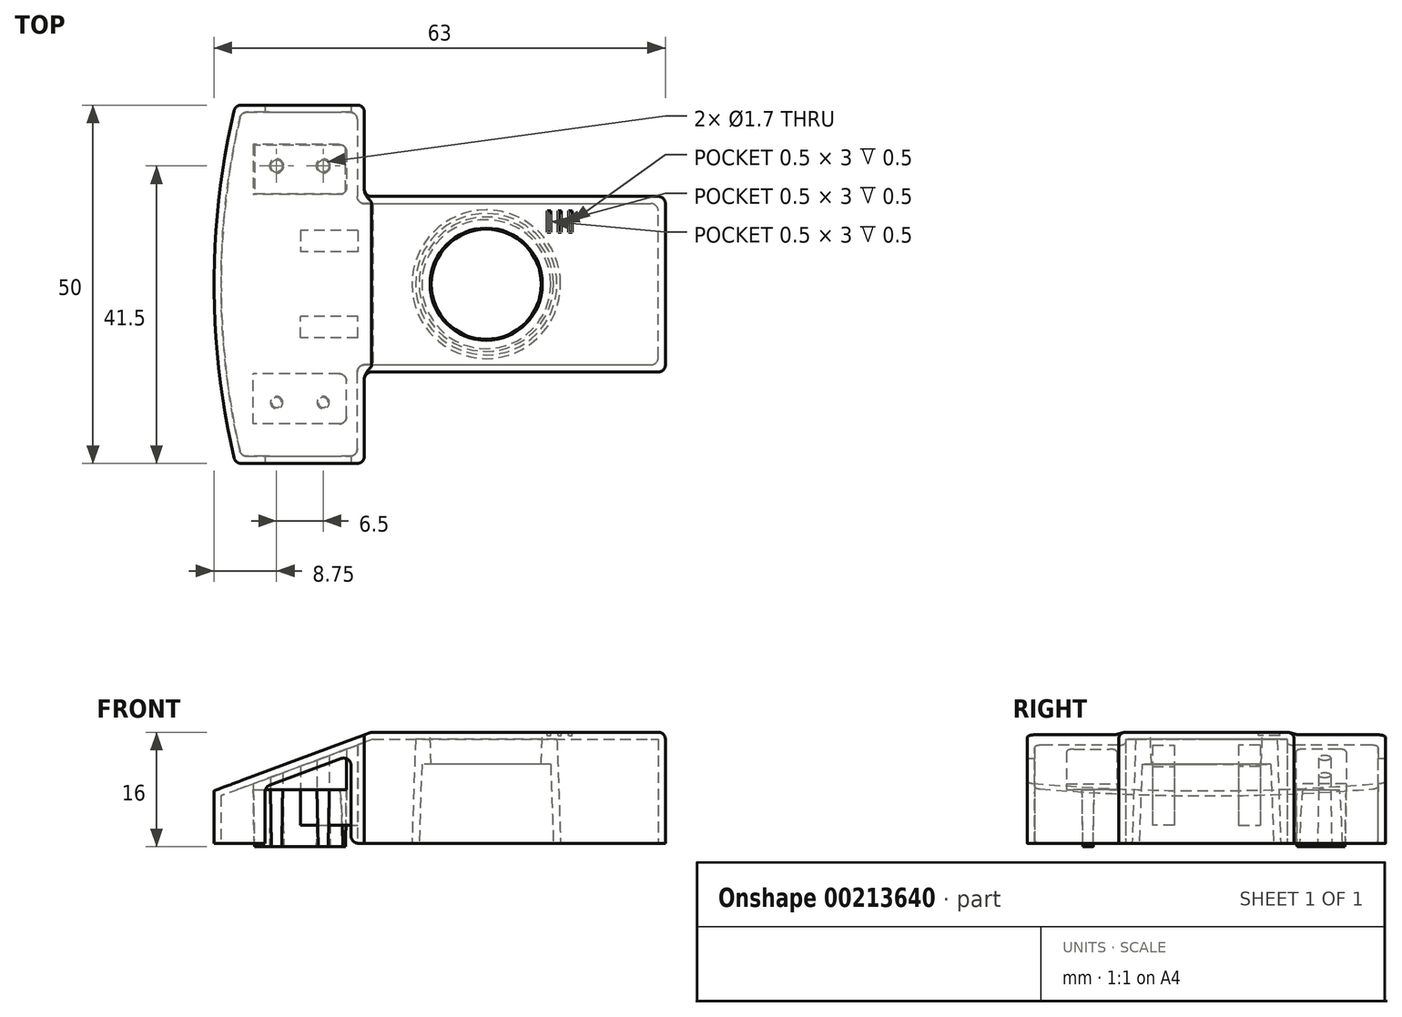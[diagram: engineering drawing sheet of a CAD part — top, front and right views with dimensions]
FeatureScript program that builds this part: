
annotation { "Feature Type Name" : "Feature", "Feature Type Description" : "" }
export const myFeature = defineFeature(function(context is Context, id is Id, definition is map)
    precondition{}
    {
        {
            var Q0;
            Q0=qCreatedBy(makeId("Top.planeOp"),FACE);
            var sketch = newSketch(context, id + "F0", { "sketchPlane" : qUnion([Q0])});
            skCircle(sketch, "E0", {"center": v(-4, 0) * mm, "radius": 9.37 * mm});
            skLineSegment(sketch, "E1.bottom", {"start": v(-21, -12.25) * mm, "end": v(21, -12.25) * mm});
            skLineSegment(sketch, "E1.top", {"start": v(-21, 12.25) * mm, "end": v(21, 12.25) * mm});
            skLineSegment(sketch, "E1.right", {"start": v(21, -12.25) * mm, "end": v(21, 12.25) * mm});
            skLineSegment(sketch, "E2.bottom", {"start": v(-21, -25) * mm, "end": v(-39, -25) * mm});
            skLineSegment(sketch, "E2.top", {"start": v(-21, 25) * mm, "end": v(-39, 25) * mm});
            skLineSegment(sketch, "E2.left", {"start": v(-21, -25) * mm, "end": v(-21, -12.25) * mm});
            skLineSegment(sketch, "E2.right", {"start": v(-39, -25) * mm, "end": v(-39, 25) * mm});
            skPoint(sketch, "E2.middle", {"position": v(-30, 0) * mm});
            skLineSegment(sketch, "E3.trimOffspring", {"start": v(-21, 12.25) * mm, "end": v(-21, 25) * mm});
            skLineSegment(sketch, "E4", {"start": v(-20, 12.25) * mm, "end": v(-20, -12.25) * mm});
            skPoint(sketch, "E5", {"position": v(-42, 0) * mm});
            skPoint(sketch, "E5.positionSnap0", {"position": v(-39, 0) * mm});
            skArc(sketch, "E6", {"start": v(-39, 25) * mm, "mid": v(-42, 0) * mm, "end": v(-39, -25) * mm});
            skSolve(sketch);
        }
        {
            var Q0;
            Q0=qSketchRegion(id+"F0",true);
            var Q1;
            Q1=makeQuery(id+"F0.imprint","IMPRINT",FACE,{"disambiguationData":[TD([[makeQuery(id+"F0.imprint","IMPRINT",EDGE,{"derivedFrom":sQuery(id+"F0.wireOp",EDGE,"E0")}),1.0]])]});
            extrude(context, id + "F1", {"entities" : qUnion([Q0, Q1]), "depth" : 15.5 * mm});
        }
        {
            var Q0;
            Q0=makeQuery(id+"F0.imprint","IMPRINT",FACE,{"disambiguationData":[TD([[makeQuery(id+"F0.imprint","IMPRINT",EDGE,{"derivedFrom":sQuery(id+"F0.wireOp",EDGE,"E0")}),1.0]])]});
            var Q1;
            Q1=makeQuery(id+"F1.opExtrude","CAP_FACE",FACE,{"disambiguationData":[OSD([sQuery(id+"F0.wireOp",EDGE,"E1.bottom"),sQuery(id+"F0.wireOp",EDGE,"E1.top"),sQuery(id+"F0.wireOp",EDGE,"E1.right"),sQuery(id+"F0.wireOp",EDGE,"E2.bottom"),sQuery(id+"F0.wireOp",EDGE,"E2.top"),sQuery(id+"F0.wireOp",EDGE,"E2.left"),sQuery(id+"F0.wireOp",EDGE,"E3.trimOffspring"),sQuery(id+"F0.wireOp",EDGE,"E6")])],"isStart":false});
            extrude(context, id + "F2", {"entities" : qUnion([Q0]), "operationType" : NewBodyOperationType.REMOVE, "endBound" : BoundingType.UP_TO_SURFACE, "endBoundEntityFace" : qUnion([Q1]), "depth" : 25 * mm, "hasDraft" : true, "draftAngle" : 2 * degree, "draftPullDirection" : true});
        }
        {
            var Q0;
            Q0=qCreatedBy(makeId("Front.planeOp"),FACE);
            var Q1;
            Q1=makeQuery(id+"F1.opExtrude","CAP_EDGE",EDGE,{"disambiguationData":[OSD([sQuery(id+"F0.wireOp",EDGE,"E2.bottom")])],"isStart":true});
            cPlane(context, id + "F3", {"entities" : qUnion([Q0, Q1]), "cplaneType" : CPlaneType.LINE_ANGLE, "offset" : 25 * mm, "angle" : 0 * degree, "width" : 150 * mm, "height" : 150 * mm});
        }
        {
            var Q0;
            Q0=qCreatedBy(id+"F3.planeOp",FACE);
            var sketch = newSketch(context, id + "F4", { "sketchPlane" : qUnion([Q0])});
            skLineSegment(sketch, "E7", {"start": v(20, 15.5) * mm, "end": v(42, 15.5) * mm});
            skLineSegment(sketch, "E8", {"start": v(42, 15.5) * mm, "end": v(42, 7.32) * mm});
            skLineSegment(sketch, "E9", {"start": v(42, 7.32) * mm, "end": v(20, 15.5) * mm});
            skLineSegment(sketch, "E10", {"start": v(42, 0) * mm, "end": v(41.46, 15.5) * mm, "construction": true});
            skLineSegment(sketch, "E11", {"start": v(42, 0) * mm, "end": v(42, 27.73) * mm, "construction": true});
            skSolve(sketch);
        }
        {
            var Q0;
            Q0=qSketchRegion(id+"F4",true);
            extrude(context, id + "F5", {"entities" : qUnion([Q0]), "operationType" : NewBodyOperationType.REMOVE, "endBound" : BoundingType.THROUGH_ALL, "depth" : 25 * mm});
        }
        {
            var Q0;
            Q0=makeQuery(id+"F1.opExtrude","CAP_FACE",FACE,{"disambiguationData":[OSD([sQuery(id+"F0.wireOp",EDGE,"E1.bottom"),sQuery(id+"F0.wireOp",EDGE,"E1.top"),sQuery(id+"F0.wireOp",EDGE,"E1.right"),sQuery(id+"F0.wireOp",EDGE,"E2.bottom"),sQuery(id+"F0.wireOp",EDGE,"E2.top"),sQuery(id+"F0.wireOp",EDGE,"E2.left"),sQuery(id+"F0.wireOp",EDGE,"E3.trimOffspring"),sQuery(id+"F0.wireOp",EDGE,"E6")])],"isStart":true});
            shell(context, id + "F6", {"entities" : qUnion([Q0]), "thickness" : 1 * mm});
        }
        {
            var Q0;
            Q0=makeQuery(id+"F1.opExtrude","SWEPT_FACE",FACE,{"disambiguationData":[OSD([sQuery(id+"F0.wireOp",EDGE,"E2.bottom")])]});
            var sketch = newSketch(context, id + "F7", { "sketchPlane" : qUnion([Q0])});
            skLineSegment(sketch, "E12", {"start": v(-20, 15.5) * mm, "end": v(-39, 8.43) * mm});
            skLineSegment(sketch, "E13", {"start": v(-39, 8.43) * mm, "end": v(-39, 15.5) * mm});
            skLineSegment(sketch, "E14", {"start": v(-39, 15.5) * mm, "end": v(-20, 15.5) * mm});
            skLineSegment(sketch, "E15", {"start": v(-34.87, 0) * mm, "end": v(-34.87, 7.86) * mm});
            skLineSegment(sketch, "E16", {"start": v(-34.87, 7.86) * mm, "end": v(-22.87, 12.32) * mm});
            skLineSegment(sketch, "E17", {"start": v(-22.87, 0) * mm, "end": v(-34.87, 0) * mm});
            skLineSegment(sketch, "E18", {"start": v(-22.87, 12.32) * mm, "end": v(-22.87, 0) * mm});
            skSolve(sketch);
        }
        {
            var Q0;
            Q0=makeQuery(id+"F7.imprint","IMPRINT",FACE,{"disambiguationData":[TD([[makeQuery(id+"F7.imprint","IMPRINT",EDGE,{"derivedFrom":sQuery(id+"F7.wireOp",EDGE,"E15")}),-1.0]])]});
            extrude(context, id + "F8", {"entities" : qUnion([Q0]), "operationType" : NewBodyOperationType.REMOVE, "endBound" : BoundingType.THROUGH_ALL, "oppositeDirection" : true, "depth" : 25 * mm});
        }
        {
            var Q0;
            Q0=makeQuery(id+"F1.opExtrude","CAP_FACE",FACE,{"disambiguationData":[OSD([sQuery(id+"F0.wireOp",EDGE,"E0"),sQuery(id+"F0.wireOp",EDGE,"E1.bottom"),sQuery(id+"F0.wireOp",EDGE,"E1.top"),sQuery(id+"F0.wireOp",EDGE,"E1.right"),sQuery(id+"F0.wireOp",EDGE,"E2.bottom"),sQuery(id+"F0.wireOp",EDGE,"E2.top"),sQuery(id+"F0.wireOp",EDGE,"E2.left"),sQuery(id+"F0.wireOp",EDGE,"E2.right"),sQuery(id+"F0.wireOp",EDGE,"E3.trimOffspring")])],"isStart":false});
            cPlane(context, id + "F9", {"entities" : qUnion([Q0]), "cplaneType" : CPlaneType.OFFSET, "offset" : 8 * mm, "oppositeDirection" : true, "width" : 150 * mm, "height" : 150 * mm});
        }
        {
            var Q0;
            Q0=qCreatedBy(id+"F9.planeOp",FACE);
            var sketch = newSketch(context, id + "F10", { "sketchPlane" : qUnion([Q0])});
            skLineSegment(sketch, "E19", {"start": v(0, 0) * mm, "end": v(-63, 0) * mm, "construction": true});
            skLineSegment(sketch, "E20.bottom", {"start": v(-36.5, -12.5) * mm, "end": v(-23.5, -12.5) * mm});
            skLineSegment(sketch, "E20.top", {"start": v(-36.5, -19.5) * mm, "end": v(-23.5, -19.5) * mm});
            skLineSegment(sketch, "E20.left", {"start": v(-36.5, -12.5) * mm, "end": v(-36.5, -19.5) * mm});
            skLineSegment(sketch, "E20.right", {"start": v(-23.5, -12.5) * mm, "end": v(-23.5, -19.5) * mm});
            skPoint(sketch, "E20.middle", {"position": v(-30, -16) * mm});
            skPoint(sketch, "E21", {"position": v(-33.25, -16.5) * mm});
            skPoint(sketch, "E22", {"position": v(-26.75, -16.5) * mm});
            skCircle(sketch, "E23", {"center": v(-33.25, -16.5) * mm, "radius": 0.85 * mm});
            skCircle(sketch, "E24", {"center": v(-26.75, -16.5) * mm, "radius": 0.85 * mm});
            skLineSegment(sketch, "E25.MirrorCS", {"start": v(-36.5, 12.5) * mm, "end": v(-23.5, 12.5) * mm});
            skLineSegment(sketch, "E26.MirrorCS", {"start": v(-36.5, 12.5) * mm, "end": v(-36.5, 19.5) * mm});
            skLineSegment(sketch, "E27.MirrorCS", {"start": v(-36.5, 19.5) * mm, "end": v(-23.5, 19.5) * mm});
            skLineSegment(sketch, "E28.MirrorCS", {"start": v(-23.5, 12.5) * mm, "end": v(-23.5, 19.5) * mm});
            skCircle(sketch, "E29.MirrorC", {"center": v(-26.75, 16.5) * mm, "radius": 0.85 * mm});
            skCircle(sketch, "E30.MirrorC", {"center": v(-33.25, 16.5) * mm, "radius": 0.85 * mm});
            skSolve(sketch);
        }
        {
            var Q0;
            Q0=makeQuery(id+"F10.imprint","IMPRINT",FACE,{"disambiguationData":[TD([[makeQuery(id+"F10.imprint","IMPRINT",EDGE,{"derivedFrom":sQuery(id+"F10.wireOp",EDGE,"E20.bottom")}),-1.0]])]});
            var Q1;
            Q1=makeQuery(id+"F10.imprint","IMPRINT",FACE,{"disambiguationData":[TD([[makeQuery(id+"F10.imprint","IMPRINT",EDGE,{"derivedFrom":sQuery(id+"F10.wireOp",EDGE,"E23")}),1.0]])]});
            var Q2;
            Q2=makeQuery(id+"F10.imprint","IMPRINT",FACE,{"disambiguationData":[TD([[makeQuery(id+"F10.imprint","IMPRINT",EDGE,{"derivedFrom":sQuery(id+"F10.wireOp",EDGE,"E24")}),1.0]])]});
            var Q3;
            Q3=makeQuery(id+"F10.imprint","IMPRINT",FACE,{"disambiguationData":[TD([[makeQuery(id+"F10.imprint","IMPRINT",EDGE,{"derivedFrom":sQuery(id+"F10.wireOp",EDGE,"E25.MirrorCS")}),1.0]])]});
            var Q4;
            Q4=makeQuery(id+"F10.imprint","IMPRINT",FACE,{"disambiguationData":[TD([[makeQuery(id+"F10.imprint","IMPRINT",EDGE,{"derivedFrom":sQuery(id+"F10.wireOp",EDGE,"E30.MirrorC")}),-1.0]])]});
            var Q5;
            Q5=makeQuery(id+"F10.imprint","IMPRINT",FACE,{"disambiguationData":[TD([[makeQuery(id+"F10.imprint","IMPRINT",EDGE,{"derivedFrom":sQuery(id+"F10.wireOp",EDGE,"E29.MirrorC")}),-1.0]])]});
            var Q6;
            Q6=makeQuery(id+"F6.opShell","OFFSET_FACE",FACE,{"disambiguationData":[OSD([sQuery(id+"F4.wireOp",EDGE,"E9")])]});
            extrude(context, id + "F11", {"entities" : qUnion([Q0, Q1, Q2, Q3, Q4, Q5]), "operationType" : NewBodyOperationType.ADD, "endBound" : BoundingType.UP_TO_SURFACE, "endBoundEntityFace" : qUnion([Q6]), "depth" : 25 * mm});
        }
        {
            var Q0;
            Q0=makeQuery(id+"F10.imprint","IMPRINT",FACE,{"disambiguationData":[TD([[makeQuery(id+"F10.imprint","IMPRINT",EDGE,{"derivedFrom":sQuery(id+"F10.wireOp",EDGE,"E23")}),1.0]])]});
            var Q1;
            Q1=makeQuery(id+"F10.imprint","IMPRINT",FACE,{"disambiguationData":[TD([[makeQuery(id+"F10.imprint","IMPRINT",EDGE,{"derivedFrom":sQuery(id+"F10.wireOp",EDGE,"E29.MirrorC")}),-1.0]])]});
            var Q2;
            Q2=makeQuery(id+"F10.imprint","IMPRINT",FACE,{"disambiguationData":[TD([[makeQuery(id+"F10.imprint","IMPRINT",EDGE,{"derivedFrom":sQuery(id+"F10.wireOp",EDGE,"E30.MirrorC")}),-1.0]])]});
            var Q3;
            Q3=makeQuery(id+"F10.imprint","IMPRINT",FACE,{"disambiguationData":[TD([[makeQuery(id+"F10.imprint","IMPRINT",EDGE,{"derivedFrom":sQuery(id+"F10.wireOp",EDGE,"E24")}),1.0]])]});
            extrude(context, id + "F12", {"entities" : qUnion([Q0, Q1, Q2, Q3]), "operationType" : NewBodyOperationType.ADD, "oppositeDirection" : true, "depth" : 8 * mm, "hasDraft" : true, "draftAngle" : 1 * degree, "draftPullDirection" : true});
        }
        {
            var Q0;
            Q0=makeQuery(id+"F1.opExtrude","CAP_EDGE",EDGE,{"disambiguationData":[OSD([sQuery(id+"F0.wireOp",EDGE,"E1.bottom")])],"isStart":false});
            var Q1;
            Q1=makeQuery(id+"F1.opExtrude","CAP_EDGE",EDGE,{"disambiguationData":[OSD([sQuery(id+"F0.wireOp",EDGE,"E1.right")])],"isStart":false});
            var Q2;
            Q2=makeQuery(id+"F1.opExtrude","CAP_EDGE",EDGE,{"disambiguationData":[OSD([sQuery(id+"F0.wireOp",EDGE,"E1.top")])],"isStart":false});
            var Q3;
            Q3=makeQuery(id+"F1.opExtrude","SWEPT_EDGE",EDGE,{"disambiguationData":[OSD([sQuery(id+"F0.wireOp",EDGE,"E1.bottom"),sQuery(id+"F0.wireOp",EDGE,"E1.right")])]});
            var Q4;
            Q4=makeQuery(id+"F1.opExtrude","SWEPT_EDGE",EDGE,{"disambiguationData":[OSD([sQuery(id+"F0.wireOp",EDGE,"E1.top"),sQuery(id+"F0.wireOp",EDGE,"E1.right")])]});
            fillet(context, id + "F13", {"entities" : qUnion([Q0, Q1, Q2, Q3, Q4]), "radius" : 1 * mm, "tangentPropagation" : true, "allowEdgeOverflow" : false});
        }
        {
            var Q0;
            Q0=makeQuery(id+"F1.opExtrude","SWEPT_EDGE",EDGE,{"disambiguationData":[OSD([sQuery(id+"F0.wireOp",EDGE,"E2.bottom"),sQuery(id+"F0.wireOp",EDGE,"E2.left")])]});
            var Q1;
            Q1=makeQuery(id+"F5.boolean.opBoolean","INTERSECT",EDGE,{"derivedFrom":[makeQuery(id+"F1.opExtrude","SWEPT_FACE",FACE,{"disambiguationData":[OSD([sQuery(id+"F0.wireOp",EDGE,"E2.left")])]}),makeQuery(id+"F5.opExtrude","SWEPT_FACE",FACE,{"disambiguationData":[OSD([sQuery(id+"FjstzwEYRuGCUyq_1.wireOp",EDGE,"6156deb2-2619-4c56-9df6-34b3699534c4")])]})]});
            var Q2;
            Q2=makeQuery(id+"F5.boolean.opBoolean","COPY",EDGE,{"derivedFrom":makeQuery(id+"F5.opExtrude","CAP_EDGE",EDGE,{"disambiguationData":[OSD([sQuery(id+"FjstzwEYRuGCUyq_1.wireOp",EDGE,"6156deb2-2619-4c56-9df6-34b3699534c4")])],"isStart":true})});
            var Q3;
            Q3=makeQuery(id+"F1.opExtrude","SWEPT_EDGE",EDGE,{"disambiguationData":[OSD([sQuery(id+"F0.wireOp",EDGE,"E2.bottom"),sQuery(id+"F0.wireOp",EDGE,"E2.right"),sQuery(id+"F0.wireOp",EDGE,"E6")])]});
            var Q4;
            Q4=makeQuery(id+"F5.boolean.opBoolean","INTERSECT",EDGE,{"derivedFrom":[makeQuery(id+"F1.opExtrude","SWEPT_FACE",FACE,{"disambiguationData":[OSD([sQuery(id+"F0.wireOp",EDGE,"E6")])]}),makeQuery(id+"F5.opExtrude","SWEPT_FACE",FACE,{"disambiguationData":[OSD([sQuery(id+"FjstzwEYRuGCUyq_1.wireOp",EDGE,"6156deb2-2619-4c56-9df6-34b3699534c4")])]})]});
            var Q5;
            Q5=makeQuery(id+"F5.boolean.opBoolean","INTERSECT",EDGE,{"derivedFrom":[makeQuery(id+"F1.opExtrude","SWEPT_FACE",FACE,{"disambiguationData":[OSD([sQuery(id+"F0.wireOp",EDGE,"E2.top")])]}),makeQuery(id+"F5.opExtrude","SWEPT_FACE",FACE,{"disambiguationData":[OSD([sQuery(id+"FjstzwEYRuGCUyq_1.wireOp",EDGE,"6156deb2-2619-4c56-9df6-34b3699534c4")])]})]});
            var Q6;
            Q6=makeQuery(id+"F1.opExtrude","SWEPT_EDGE",EDGE,{"disambiguationData":[OSD([sQuery(id+"F0.wireOp",EDGE,"E2.top"),sQuery(id+"F0.wireOp",EDGE,"E2.right"),sQuery(id+"F0.wireOp",EDGE,"E6")])]});
            var Q7;
            Q7=makeQuery(id+"F1.opExtrude","SWEPT_EDGE",EDGE,{"disambiguationData":[OSD([sQuery(id+"F0.wireOp",EDGE,"E2.top"),sQuery(id+"F0.wireOp",EDGE,"E3.trimOffspring")])]});
            var Q8;
            Q8=makeQuery(id+"F5.boolean.opBoolean","INTERSECT",EDGE,{"derivedFrom":[makeQuery(id+"F1.opExtrude","SWEPT_FACE",FACE,{"disambiguationData":[OSD([sQuery(id+"F0.wireOp",EDGE,"E3.trimOffspring")])]}),makeQuery(id+"F5.opExtrude","SWEPT_FACE",FACE,{"disambiguationData":[OSD([sQuery(id+"FjstzwEYRuGCUyq_1.wireOp",EDGE,"6156deb2-2619-4c56-9df6-34b3699534c4")])]})]});
            fillet(context, id + "F14", {"entities" : qUnion([Q0, Q1, Q2, Q3, Q4, Q5, Q6, Q7, Q8]), "radius" : 1 * mm, "tangentPropagation" : true, "allowEdgeOverflow" : false});
        }
        {
            var Q0;
            Q0=makeQuery(id+"F1.opExtrude","SWEPT_EDGE",EDGE,{"disambiguationData":[OSD([sQuery(id+"F0.wireOp",EDGE,"E1.top"),sQuery(id+"F0.wireOp",EDGE,"E3.trimOffspring")])]});
            fillet(context, id + "F15", {"entities" : qUnion([Q0]), "radius" : 1 * mm, "tangentPropagation" : true, "allowEdgeOverflow" : false});
        }
        {
            var Q0;
            Q0=makeQuery(id+"F1.opExtrude","SWEPT_EDGE",EDGE,{"disambiguationData":[OSD([sQuery(id+"F0.wireOp",EDGE,"E1.bottom"),sQuery(id+"F0.wireOp",EDGE,"E2.left")])]});
            var Q1;
            {var subQ0=sQuery(id+"F0.wireOp",EDGE,"E2.bottom");var subQ1=sQuery(id+"F7.wireOp",EDGE,"E18");Q1=makeQuery(id+"F8.boolean.opBoolean","COPY",EDGE,{"disambiguationData":[TD([makeQuery(id+"F1.opExtrude","SWEPT_FACE",FACE,{"disambiguationData":[OSD([subQ0])]})])],"derivedFrom":makeQuery(id+"F8.opExtrude","SWEPT_EDGE",EDGE,{"disambiguationData":[OSD([subQ0,sQuery(id+"F7.wireOp",EDGE,"E17"),subQ1])]})});}
            var Q2;
            {var subQ0=sQuery(id+"F0.wireOp",EDGE,"E2.bottom");var subQ1=sQuery(id+"F7.wireOp",EDGE,"E15");Q2=makeQuery(id+"F8.boolean.opBoolean","COPY",EDGE,{"disambiguationData":[TD([makeQuery(id+"F1.opExtrude","SWEPT_FACE",FACE,{"disambiguationData":[OSD([subQ0])]})])],"derivedFrom":makeQuery(id+"F8.opExtrude","SWEPT_EDGE",EDGE,{"disambiguationData":[OSD([subQ0,subQ1,sQuery(id+"F7.wireOp",EDGE,"E17")])]})});}
            var Q3;
            {var subQ0=sQuery(id+"F0.wireOp",EDGE,"E2.top");var subQ1=sQuery(id+"F0.wireOp",EDGE,"E2.bottom");var subQ2=sQuery(id+"F7.wireOp",EDGE,"E15");Q3=makeQuery(id+"F8.boolean.opBoolean","COPY",EDGE,{"disambiguationData":[TD([makeQuery(id+"F1.opExtrude","SWEPT_FACE",FACE,{"disambiguationData":[OSD([subQ0])]})])],"derivedFrom":makeQuery(id+"F8.opExtrude","SWEPT_EDGE",EDGE,{"disambiguationData":[OSD([subQ1,subQ2,sQuery(id+"F7.wireOp",EDGE,"E17")])]})});}
            var Q4;
            {var subQ0=sQuery(id+"F0.wireOp",EDGE,"E2.top");var subQ1=sQuery(id+"F0.wireOp",EDGE,"E2.bottom");var subQ2=sQuery(id+"F7.wireOp",EDGE,"E18");Q4=makeQuery(id+"F8.boolean.opBoolean","COPY",EDGE,{"disambiguationData":[TD([makeQuery(id+"F1.opExtrude","SWEPT_FACE",FACE,{"disambiguationData":[OSD([subQ0])]})])],"derivedFrom":makeQuery(id+"F8.opExtrude","SWEPT_EDGE",EDGE,{"disambiguationData":[OSD([subQ1,sQuery(id+"F7.wireOp",EDGE,"E17"),subQ2])]})});}
            var Q5;
            {var subQ0=sQuery(id+"F0.wireOp",EDGE,"E2.top");var subQ1=sQuery(id+"F7.wireOp",EDGE,"E18");var subQ2=sQuery(id+"F7.wireOp",EDGE,"E16");Q5=makeQuery(id+"F8.boolean.opBoolean","COPY",EDGE,{"disambiguationData":[TD([makeQuery(id+"F1.opExtrude","SWEPT_FACE",FACE,{"disambiguationData":[OSD([subQ0])]})])],"derivedFrom":makeQuery(id+"F8.opExtrude","SWEPT_EDGE",EDGE,{"disambiguationData":[OSD([subQ2,subQ1])]})});}
            var Q6;
            {var subQ0=sQuery(id+"F0.wireOp",EDGE,"E2.top");var subQ1=sQuery(id+"F7.wireOp",EDGE,"E15");var subQ2=sQuery(id+"F7.wireOp",EDGE,"E16");Q6=makeQuery(id+"F8.boolean.opBoolean","COPY",EDGE,{"disambiguationData":[TD([makeQuery(id+"F1.opExtrude","SWEPT_FACE",FACE,{"disambiguationData":[OSD([subQ0])]})])],"derivedFrom":makeQuery(id+"F8.opExtrude","SWEPT_EDGE",EDGE,{"disambiguationData":[OSD([subQ1,subQ2])]})});}
            var Q7;
            {var subQ0=sQuery(id+"F0.wireOp",EDGE,"E2.bottom");var subQ1=sQuery(id+"F7.wireOp",EDGE,"E18");var subQ2=sQuery(id+"F7.wireOp",EDGE,"E16");Q7=makeQuery(id+"F8.boolean.opBoolean","COPY",EDGE,{"disambiguationData":[TD([makeQuery(id+"F1.opExtrude","SWEPT_FACE",FACE,{"disambiguationData":[OSD([subQ0])]})])],"derivedFrom":makeQuery(id+"F8.opExtrude","SWEPT_EDGE",EDGE,{"disambiguationData":[OSD([subQ2,subQ1])]})});}
            var Q8;
            {var subQ0=sQuery(id+"F0.wireOp",EDGE,"E2.bottom");var subQ1=sQuery(id+"F7.wireOp",EDGE,"E15");var subQ2=sQuery(id+"F7.wireOp",EDGE,"E16");Q8=makeQuery(id+"F8.boolean.opBoolean","COPY",EDGE,{"disambiguationData":[TD([makeQuery(id+"F1.opExtrude","SWEPT_FACE",FACE,{"disambiguationData":[OSD([subQ0])]})])],"derivedFrom":makeQuery(id+"F8.opExtrude","SWEPT_EDGE",EDGE,{"disambiguationData":[OSD([subQ1,subQ2])]})});}
            var Q9;
            Q9=makeQuery(id+"F6.opShell","OFFSET_EDGE",EDGE,{"disambiguationData":[OSD([sQuery(id+"F0.wireOp",EDGE,"E1.top"),sQuery(id+"F0.wireOp",EDGE,"E3.trimOffspring")])]});
            var Q10;
            Q10=makeQuery(id+"F6.opShell","OFFSET_EDGE",EDGE,{"disambiguationData":[OSD([sQuery(id+"F0.wireOp",EDGE,"E1.bottom"),sQuery(id+"F0.wireOp",EDGE,"E2.left")])]});
            fillet(context, id + "F16", {"entities" : qUnion([Q0, Q1, Q2, Q3, Q4, Q5, Q6, Q7, Q8, Q9, Q10]), "radius" : 1 * mm, "tangentPropagation" : true, "allowEdgeOverflow" : false});
        }
        {
            var Q0;
            Q0=makeQuery(id+"F6.opShell","OFFSET_EDGE",EDGE,{"disambiguationData":[OSD([sQuery(id+"F0.wireOp",EDGE,"E1.top"),sQuery(id+"F0.wireOp",EDGE,"E1.right")])]});
            var Q1;
            Q1=makeQuery(id+"F6.opShell","OFFSET_EDGE",EDGE,{"disambiguationData":[OSD([sQuery(id+"F0.wireOp",EDGE,"E1.bottom"),sQuery(id+"F0.wireOp",EDGE,"E1.right")])]});
            var Q2;
            {var subQ0=sQuery(id+"F0.wireOp",EDGE,"E0");Q2=makeQuery(id+"F6.opShell","OFFSET_EDGE",EDGE,{"disambiguationData":[OSD([subQ0]),TDD([makeQuery(id+"F1.opExtrude","CAP_EDGE",EDGE,{"disambiguationData":[OSD([subQ0])],"isStart":false})])]});}
            var Q3;
            Q3=makeQuery(id+"F6.opShell","OFFSET_EDGE",EDGE,{"disambiguationData":[OSD([sQuery(id+"F0.wireOp",EDGE,"E2.top"),sQuery(id+"F0.wireOp",EDGE,"E3.trimOffspring")])]});
            var Q4;
            Q4=makeQuery(id+"F6.opShell","OFFSET_EDGE",EDGE,{"disambiguationData":[OSD([sQuery(id+"F0.wireOp",EDGE,"E2.top"),sQuery(id+"F0.wireOp",EDGE,"E2.right"),sQuery(id+"F0.wireOp",EDGE,"E6")])]});
            var Q5;
            Q5=makeQuery(id+"F6.opShell","OFFSET_EDGE",EDGE,{"disambiguationData":[OSD([sQuery(id+"F0.wireOp",EDGE,"E2.bottom"),sQuery(id+"F0.wireOp",EDGE,"E2.left")])]});
            var Q6;
            Q6=makeQuery(id+"F6.opShell","OFFSET_EDGE",EDGE,{"disambiguationData":[OSD([sQuery(id+"F0.wireOp",EDGE,"E2.bottom"),sQuery(id+"F0.wireOp",EDGE,"E2.right"),sQuery(id+"F0.wireOp",EDGE,"E6")])]});
            var Q7;
            Q7=makeQuery(id+"F11.opExtrude","SWEPT_EDGE",EDGE,{"disambiguationData":[OSD([sQuery(id+"F10.wireOp",EDGE,"E20.bottom"),sQuery(id+"F10.wireOp",EDGE,"E20.right")])]});
            var Q8;
            Q8=makeQuery(id+"F11.opExtrude","SWEPT_EDGE",EDGE,{"disambiguationData":[OSD([sQuery(id+"F10.wireOp",EDGE,"E20.top"),sQuery(id+"F10.wireOp",EDGE,"E20.right")])]});
            var Q9;
            Q9=makeQuery(id+"F11.opExtrude","SWEPT_EDGE",EDGE,{"disambiguationData":[OSD([sQuery(id+"F10.wireOp",EDGE,"E27.MirrorCS"),sQuery(id+"F10.wireOp",EDGE,"E28.MirrorCS")])]});
            var Q10;
            Q10=makeQuery(id+"F11.opExtrude","SWEPT_EDGE",EDGE,{"disambiguationData":[OSD([sQuery(id+"F10.wireOp",EDGE,"E25.MirrorCS"),sQuery(id+"F10.wireOp",EDGE,"E28.MirrorCS")])]});
            fillet(context, id + "F17", {"entities" : qUnion([Q0, Q1, Q2, Q3, Q4, Q5, Q6, Q7, Q8, Q9, Q10]), "radius" : 1 * mm, "tangentPropagation" : true, "allowEdgeOverflow" : false});
        }
        {
            var Q0;
            Q0=qCreatedBy(id+"F9.planeOp",FACE);
            var sketch = newSketch(context, id + "F18", { "sketchPlane" : qUnion([Q0])});
            skPoint(sketch, "E31", {"position": v(-29.94, -4.5) * mm});
            skLineSegment(sketch, "E32.bottom", {"start": v(-29.94, -4.5) * mm, "end": v(-21.94, -4.5) * mm});
            skLineSegment(sketch, "E32.top", {"start": v(-29.94, -7.5) * mm, "end": v(-21.94, -7.5) * mm});
            skLineSegment(sketch, "E32.left", {"start": v(-29.94, -4.5) * mm, "end": v(-29.94, -7.5) * mm});
            skLineSegment(sketch, "E32.right", {"start": v(-21.94, -4.5) * mm, "end": v(-21.94, -7.5) * mm});
            skLineSegment(sketch, "E33", {"start": v(0, 0) * mm, "end": v(-48.4, 0) * mm, "construction": true});
            skLineSegment(sketch, "E34.MirrorCS", {"start": v(-29.94, 4.5) * mm, "end": v(-21.94, 4.5) * mm});
            skLineSegment(sketch, "E35.MirrorCS", {"start": v(-21.94, 4.5) * mm, "end": v(-21.94, 7.5) * mm});
            skLineSegment(sketch, "E36.MirrorCS", {"start": v(-29.94, 7.5) * mm, "end": v(-21.94, 7.5) * mm});
            skLineSegment(sketch, "E37.MirrorCS", {"start": v(-29.94, 4.5) * mm, "end": v(-29.94, 7.5) * mm});
            skSolve(sketch);
        }
        {
            var Q0;
            Q0=qSketchRegion(id+"F18",true);
            var Q1;
            Q1=makeQuery(id+"F6.opShell","OFFSET_FACE",FACE,{"disambiguationData":[OSD([sQuery(id+"F4.wireOp",EDGE,"E9")])]});
            extrude(context, id + "F19", {"entities" : qUnion([Q0]), "operationType" : NewBodyOperationType.ADD, "endBound" : BoundingType.UP_TO_SURFACE, "endBoundEntityFace" : qUnion([Q1]), "depth" : 25 * mm, "hasSecondDirection" : true, "secondDirectionOppositeDirection" : true, "secondDirectionDepth" : 5 * mm});
        }
        {
            var Q0;
            Q0=makeQuery(id+"F1.opExtrude","CAP_FACE",FACE,{"disambiguationData":[OSD([sQuery(id+"F0.wireOp",EDGE,"E1.bottom"),sQuery(id+"F0.wireOp",EDGE,"E1.top"),sQuery(id+"F0.wireOp",EDGE,"E1.right"),sQuery(id+"F0.wireOp",EDGE,"E2.bottom"),sQuery(id+"F0.wireOp",EDGE,"E2.top"),sQuery(id+"F0.wireOp",EDGE,"E2.left"),sQuery(id+"F0.wireOp",EDGE,"E3.trimOffspring"),sQuery(id+"F0.wireOp",EDGE,"E6")])],"isStart":false});
            var sketch = newSketch(context, id + "F20", { "sketchPlane" : qUnion([Q0])});
            skCircle(sketch, "E38", {"center": v(-4, 0) * mm, "radius": 8.83 * mm});
            skCircle(sketch, "E39.0", {"center": v(-4, 0) * mm, "radius": 7.83 * mm});
            skSolve(sketch);
        }
        {
            var Q0;
            Q0 = qSketchRegion(id + "F20", true);
            extrude(context, id + "F21", {"entities" : qUnion([Q0]), "operationType" : NewBodyOperationType.ADD, "oppositeDirection" : true, "depth" : 4.5 * mm, "hasDraft" : true, "draftAngle" : 2 * degree});
        }
        {
            var Q0;
            Q0=makeQuery(id+"F21.boolean.opBoolean","MERGE",FACE,{"derivedFrom":[makeQuery(id+"F1.opExtrude","CAP_FACE",FACE,{"disambiguationData":[OSD([sQuery(id+"F0.wireOp",EDGE,"E1.bottom"),sQuery(id+"F0.wireOp",EDGE,"E1.top"),sQuery(id+"F0.wireOp",EDGE,"E1.right"),sQuery(id+"F0.wireOp",EDGE,"E2.bottom"),sQuery(id+"F0.wireOp",EDGE,"E2.top"),sQuery(id+"F0.wireOp",EDGE,"E2.left"),sQuery(id+"F0.wireOp",EDGE,"E3.trimOffspring"),sQuery(id+"F0.wireOp",EDGE,"E6")])],"isStart":false}),makeQuery(id+"F21.opExtrude","CAP_FACE",FACE,{"disambiguationData":[OSD([sQuery(id+"F20.wireOp",EDGE,"E38"),sQuery(id+"F20.wireOp",EDGE,"E39.0")])],"isStart":true})]});
            var sketch = newSketch(context, id + "F22", { "sketchPlane" : qUnion([Q0])});
            skLineSegment(sketch, "E40.bottom", {"start": v(4.5, 10.25) * mm, "end": v(8, 10.25) * mm});
            skLineSegment(sketch, "E40.top", {"start": v(4.5, 7.25) * mm, "end": v(8, 7.25) * mm});
            skLineSegment(sketch, "E40.left", {"start": v(4.5, 10.25) * mm, "end": v(4.5, 7.25) * mm});
            skLineSegment(sketch, "E40.right", {"start": v(8, 10.25) * mm, "end": v(8, 7.25) * mm});
            skLineSegment(sketch, "E41", {"start": v(5, 10.25) * mm, "end": v(5, 7.25) * mm});
            skLineSegment(sketch, "E42", {"start": v(6, 10.25) * mm, "end": v(6, 7.25) * mm});
            skPoint(sketch, "E42.endSnap0", {"position": v(6.25, 7.25) * mm});
            skLineSegment(sketch, "E43", {"start": v(6.5, 10.25) * mm, "end": v(6.5, 7.25) * mm});
            skLineSegment(sketch, "E44", {"start": v(7.5, 10.25) * mm, "end": v(7.5, 7.25) * mm});
            skSolve(sketch);
        }
        {
            var Q0;
            {var subQ0=sQuery(id+"F22.wireOp",EDGE,"E40.left");Q0=makeQuery(id+"F22.imprint","IMPRINT",FACE,{"disambiguationData":[TD([[makeQuery(id+"F22.imprint","IMPRINT",EDGE,{"derivedFrom":subQ0}),1.0]])]});}
            var Q1;
            {var subQ0=sQuery(id+"F22.wireOp",EDGE,"E42");Q1=makeQuery(id+"F22.imprint","IMPRINT",FACE,{"disambiguationData":[TD([[makeQuery(id+"F22.imprint","IMPRINT",EDGE,{"derivedFrom":subQ0}),1.0]])]});}
            var Q2;
            {var subQ0=sQuery(id+"F22.wireOp",EDGE,"E40.right");Q2=makeQuery(id+"F22.imprint","IMPRINT",FACE,{"disambiguationData":[TD([[makeQuery(id+"F22.imprint","IMPRINT",EDGE,{"derivedFrom":subQ0}),-1.0]])]});}
            extrude(context, id + "F23", {"entities" : qUnion([Q0, Q1, Q2]), "operationType" : NewBodyOperationType.REMOVE, "oppositeDirection" : true, "depth" : 0.5 * mm});
        }
    });
